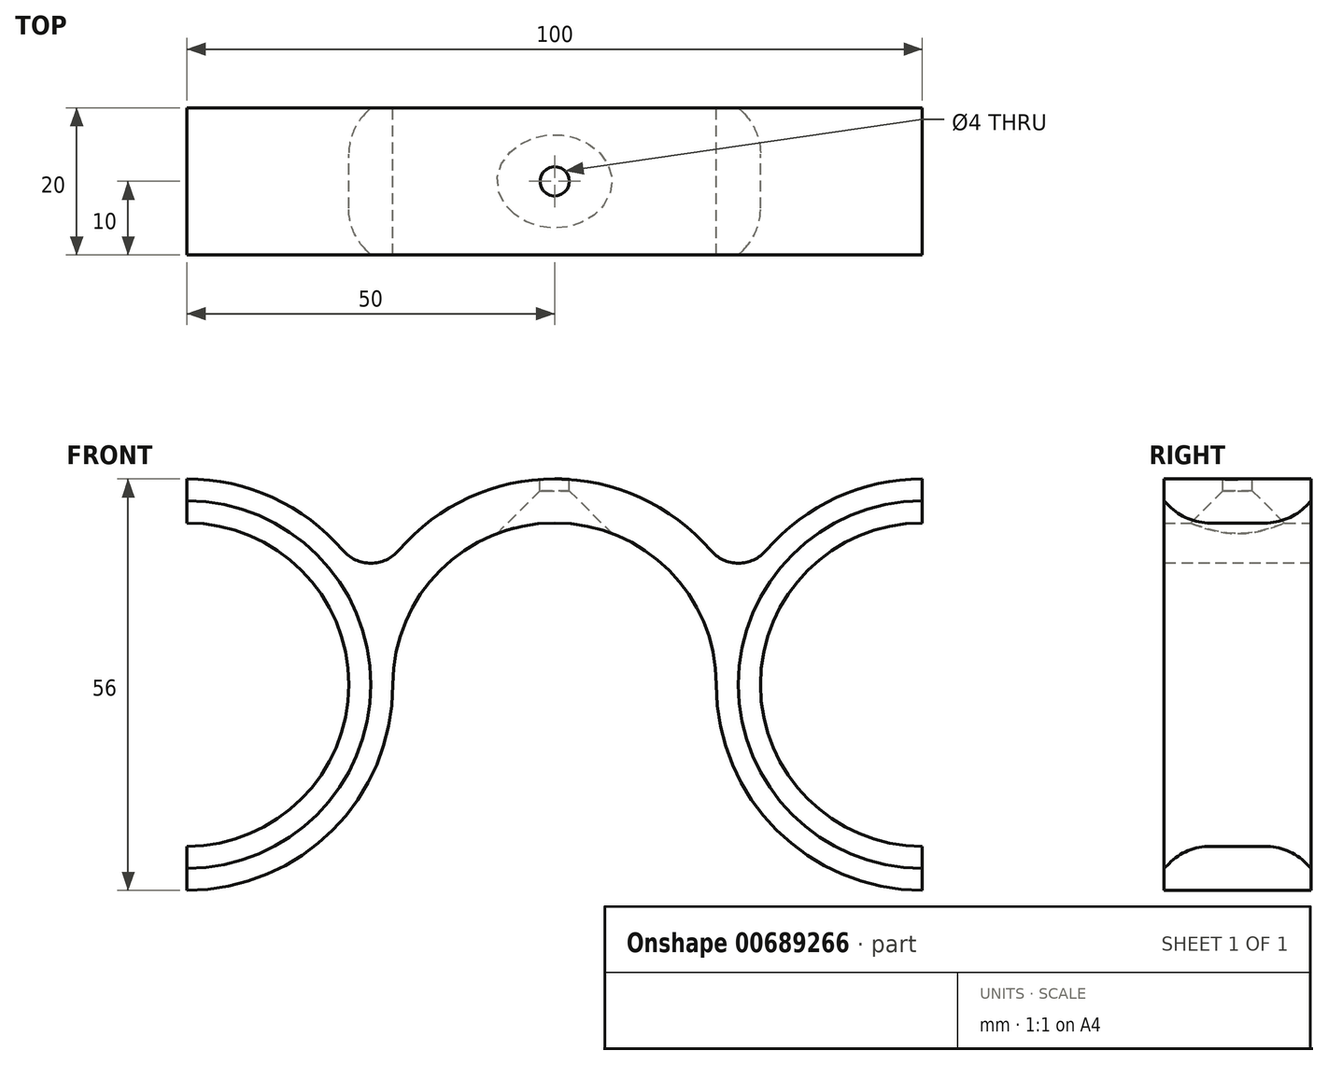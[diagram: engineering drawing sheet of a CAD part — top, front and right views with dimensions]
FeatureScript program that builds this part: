
annotation { "Feature Type Name" : "Feature", "Feature Type Description" : "" }
export const myFeature = defineFeature(function(context is Context, id is Id, definition is map)
    precondition{}
    {
        {
            var Q0;
            Q0=qCreatedBy(makeId("Front.planeOp"),FACE);
            var sketch = newSketch(context, id + "F0", { "sketchPlane" : qUnion([Q0])});
            skArc(sketch, "E0", {"start": v(-50, -22) * mm, "mid": v(-28, 0) * mm, "end": v(-50, 22) * mm});
            skLineSegment(sketch, "E1", {"start": v(0, 0) * mm, "end": v(0, 28) * mm, "construction": true});
            skLineSegment(sketch, "E2", {"start": v(-50, 0) * mm, "end": v(-50, 22) * mm, "construction": true});
            skLineSegment(sketch, "E3", {"start": v(-50, 22) * mm, "end": v(-50, 28) * mm});
            skLineSegment(sketch, "E4", {"start": v(-50, 28) * mm, "end": v(0, 28) * mm, "construction": true});
            skArc(sketch, "E5", {"start": v(-25, 12.6) * mm, "mid": v(-35.32, 23.84) * mm, "end": v(-50, 28) * mm});
            skLineSegment(sketch, "E6", {"start": v(-50, -22) * mm, "end": v(-50, -28) * mm});
            skArc(sketch, "E7.trimOffspring", {"start": v(-50, -28) * mm, "mid": v(-42.78, -27.05) * mm, "end": v(-36.06, -24.28) * mm});
            skArc(sketch, "E8.trimOffspring", {"start": v(-36.06, -24.28) * mm, "mid": v(-25.77, -14.03) * mm, "end": v(-22, 0) * mm});
            skLineSegment(sketch, "E9.MirrorCS", {"start": v(50, 22) * mm, "end": v(50, 28) * mm});
            skLineSegment(sketch, "E10.MirrorCS", {"start": v(50, -22) * mm, "end": v(50, -28) * mm});
            skArc(sketch, "E11.MirrorCS", {"start": v(50, -28) * mm, "mid": v(42.78, -27.05) * mm, "end": v(36.06, -24.28) * mm});
            skArc(sketch, "E12.MirrorCS", {"start": v(36.06, -24.28) * mm, "mid": v(25.77, -14.03) * mm, "end": v(22, 0) * mm});
            skArc(sketch, "E13.MirrorCS", {"start": v(50, -22) * mm, "mid": v(28, 0) * mm, "end": v(50, 22) * mm});
            skArc(sketch, "E14.MirrorCS", {"start": v(25, 12.6) * mm, "mid": v(35.32, 23.84) * mm, "end": v(50, 28) * mm});
            skArc(sketch, "E15.trimOffspring", {"start": v(25, 12.6) * mm, "mid": v(0, 28) * mm, "end": v(-25, 12.6) * mm});
            skArc(sketch, "E16.trimOffspring", {"start": v(22, 0) * mm, "mid": v(0, 22) * mm, "end": v(-22, 0) * mm});
            skSolve(sketch);
        }
        {
            var Q0;
            Q0 = qSketchRegion(id + "F0", true);
            extrude(context, id + "F1", {"entities" : qUnion([Q0]), "endBound" : BoundingType.SYMMETRIC, "depth" : 20 * mm, "offsetDistance" : 25 * mm});
        }
        {
            var Q0;
            Q0=qCreatedBy(makeId("Front.planeOp"),FACE);
            var sketch = newSketch(context, id + "F2", { "sketchPlane" : qUnion([Q0])});
            skLineSegment(sketch, "E17", {"start": v(0, 0) * mm, "end": v(0, 32.48) * mm, "construction": true});
            skLineSegment(sketch, "E18", {"start": v(-2, 31.63) * mm, "end": v(-2, 26.39) * mm});
            skLineSegment(sketch, "E19", {"start": v(-2, 26.39) * mm, "end": v(-8.58, 19.8) * mm});
            skLineSegment(sketch, "E20", {"start": v(-8.58, 19.8) * mm, "end": v(0, 19.8) * mm});
            skLineSegment(sketch, "E21", {"start": v(-2, 31.63) * mm, "end": v(0, 31.63) * mm});
            skLineSegment(sketch, "E22", {"start": v(0, 31.63) * mm, "end": v(0, 19.8) * mm});
            skSolve(sketch);
        }
        {
            var Q0;
            Q0 = qSketchRegion(id + "F2", true);
            var Q1;
            Q1=sQuery(id+"F2.wireOp",EDGE,"E17");
            revolve(context, id + "F3", {"operationType" : NewBodyOperationType.REMOVE, "entities" : qUnion([Q0]), "axis" : qUnion([Q1]), "revolveType" : RevolveType.FULL, "oppositeDirection" : true});
        }
        {
            var Q0;
            Q0=makeQuery(id+"F1.opExtrude","CAP_EDGE",EDGE,{"disambiguationData":[OSD([sQuery(id+"F0.wireOp",EDGE,"E0")])],"isStart":true});
            var Q1;
            Q1=makeQuery(id+"F1.opExtrude","CAP_EDGE",EDGE,{"disambiguationData":[OSD([sQuery(id+"F0.wireOp",EDGE,"E0")])],"isStart":false});
            var Q2;
            Q2=makeQuery(id+"F1.opExtrude","CAP_EDGE",EDGE,{"disambiguationData":[OSD([sQuery(id+"F0.wireOp",EDGE,"E13.MirrorCS")])],"isStart":true});
            var Q3;
            Q3=makeQuery(id+"F1.opExtrude","CAP_EDGE",EDGE,{"disambiguationData":[OSD([sQuery(id+"F0.wireOp",EDGE,"E13.MirrorCS")])],"isStart":false});
            chamfer(context, id + "F4", {"entities" : qUnion([Q0, Q1, Q2, Q3]), "width" : 3 * mm, "tangentPropagation" : true});
        }
        {
            var Q0;
            {var subQ0=sQuery(id+"F0.wireOp",EDGE,"E0");Q0=makeQuery(id+"F4.opChamfer","BLEND_EDGE",EDGE,{"blendedFrom":[makeQuery(id+"F1.opExtrude","CAP_EDGE",EDGE,{"disambiguationData":[OSD([subQ0])],"isStart":true}),makeQuery(id+"F1.opExtrude","SWEPT_FACE",FACE,{"disambiguationData":[OSD([subQ0])]})],"blendedInto":[makeQuery(id+"F1.opExtrude","SWEPT_FACE",FACE,{"disambiguationData":[OSD([subQ0])]})]});}
            var Q1;
            {var subQ0=sQuery(id+"F0.wireOp",EDGE,"E0");Q1=makeQuery(id+"F4.opChamfer","BLEND_EDGE",EDGE,{"blendedFrom":[makeQuery(id+"F1.opExtrude","CAP_EDGE",EDGE,{"disambiguationData":[OSD([subQ0])],"isStart":false}),makeQuery(id+"F1.opExtrude","SWEPT_FACE",FACE,{"disambiguationData":[OSD([subQ0])]})],"blendedInto":[makeQuery(id+"F1.opExtrude","SWEPT_FACE",FACE,{"disambiguationData":[OSD([subQ0])]})]});}
            var Q2;
            {var subQ0=sQuery(id+"F0.wireOp",EDGE,"E13.MirrorCS");Q2=makeQuery(id+"F4.opChamfer","BLEND_EDGE",EDGE,{"blendedFrom":[makeQuery(id+"F1.opExtrude","CAP_EDGE",EDGE,{"disambiguationData":[OSD([subQ0])],"isStart":true}),makeQuery(id+"F1.opExtrude","SWEPT_FACE",FACE,{"disambiguationData":[OSD([subQ0])]})],"blendedInto":[makeQuery(id+"F1.opExtrude","SWEPT_FACE",FACE,{"disambiguationData":[OSD([subQ0])]})]});}
            var Q3;
            {var subQ0=sQuery(id+"F0.wireOp",EDGE,"E13.MirrorCS");Q3=makeQuery(id+"F4.opChamfer","BLEND_EDGE",EDGE,{"blendedFrom":[makeQuery(id+"F1.opExtrude","CAP_EDGE",EDGE,{"disambiguationData":[OSD([subQ0])],"isStart":false}),makeQuery(id+"F1.opExtrude","SWEPT_FACE",FACE,{"disambiguationData":[OSD([subQ0])]})],"blendedInto":[makeQuery(id+"F1.opExtrude","SWEPT_FACE",FACE,{"disambiguationData":[OSD([subQ0])]})]});}
            fillet(context, id + "F5", {"entities" : qUnion([Q0, Q1, Q2, Q3]), "radius" : 8 * mm, "tangentPropagation" : true, "allowEdgeOverflow" : false});
        }
        {
            var Q0;
            Q0=makeQuery(id+"F1.opExtrude","SWEPT_EDGE",EDGE,{"disambiguationData":[OSD([sQuery(id+"F0.wireOp",EDGE,"E14.MirrorCS"),sQuery(id+"F0.wireOp",EDGE,"E15.trimOffspring")])]});
            var Q1;
            Q1=makeQuery(id+"F1.opExtrude","SWEPT_EDGE",EDGE,{"disambiguationData":[OSD([sQuery(id+"F0.wireOp",EDGE,"E5"),sQuery(id+"F0.wireOp",EDGE,"E15.trimOffspring")])]});
            fillet(context, id + "F6", {"entities" : qUnion([Q0, Q1]), "radius" : 5 * mm, "tangentPropagation" : true, "allowEdgeOverflow" : false});
        }
    });
